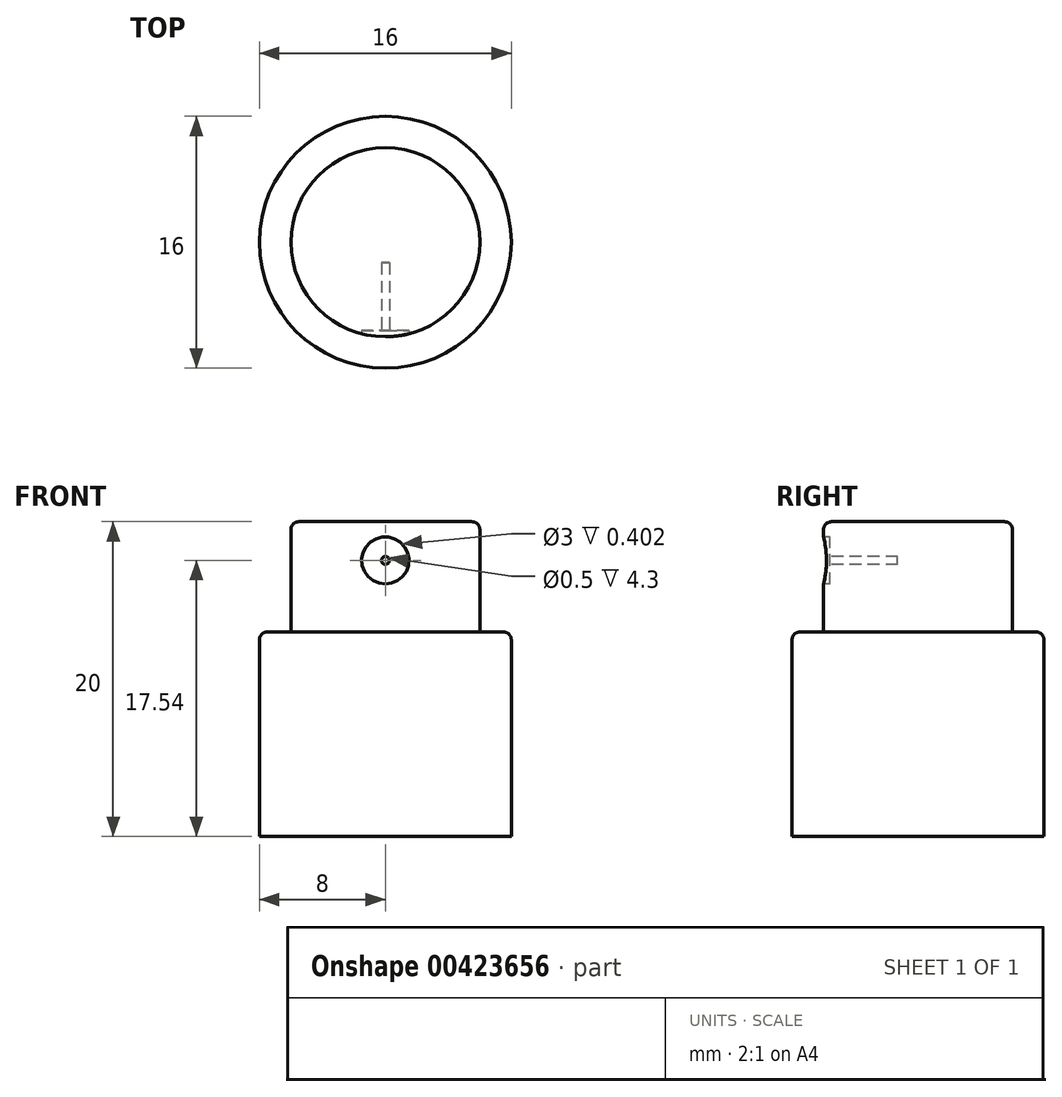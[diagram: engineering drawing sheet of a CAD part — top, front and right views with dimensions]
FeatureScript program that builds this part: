
annotation { "Feature Type Name" : "Feature", "Feature Type Description" : "" }
export const myFeature = defineFeature(function(context is Context, id is Id, definition is map)
    precondition{}
    {
        {
            var Q0;
            Q0=qCreatedBy(makeId("Top.planeOp"),FACE);
            var sketch = newSketch(context, id + "F0", { "sketchPlane" : qUnion([Q0])});
            skCircle(sketch, "E0", {"center": v(0, 0) * mm, "radius": 8 * mm});
            skCircle(sketch, "E1", {"center": v(0, 0) * mm, "radius": 6 * mm});
            skSolve(sketch);
        }
        {
            var Q0;
            Q0=makeQuery(id+"F0.imprint","IMPRINT",FACE,{"disambiguationData":[TD([[makeQuery(id+"F0.imprint","IMPRINT",EDGE,{"derivedFrom":sQuery(id+"F0.wireOp",EDGE,"E1")}),1.0]])]});
            extrude(context, id + "F1", {"entities" : qUnion([Q0]), "depth" : 20 * mm});
        }
        {
            var Q0;
            Q0=qSketchRegion(id+"F0",true);
            extrude(context, id + "F2", {"entities" : qUnion([Q0]), "operationType" : NewBodyOperationType.ADD, "depth" : 13 * mm});
        }
        {
            var Q0;
            Q0=qCreatedBy(makeId("Front.planeOp"),FACE);
            cPlane(context, id + "F3", {"entities" : qUnion([Q0]), "cplaneType" : CPlaneType.OFFSET, "offset" : 25 * mm, "width" : 150 * mm, "height" : 150 * mm});
        }
        {
            var Q0;
            Q0=qCreatedBy(id+"F3.planeOp",FACE);
            var sketch = newSketch(context, id + "F4", { "sketchPlane" : qUnion([Q0])});
            skCircle(sketch, "E2", {"center": v(0, 17.54) * mm, "radius": 1.5 * mm});
            skCircle(sketch, "E3", {"center": v(0, 17.54) * mm, "radius": 0.25 * mm});
            skSolve(sketch);
        }
        {
            var Q0;
            Q0=makeQuery(id+"F4.imprint","IMPRINT",FACE,{"disambiguationData":[TD([[makeQuery(id+"F4.imprint","IMPRINT",EDGE,{"derivedFrom":sQuery(id+"F4.wireOp",EDGE,"E3")}),1.0]])]});
            extrude(context, id + "F5", {"entities" : qUnion([Q0]), "operationType" : NewBodyOperationType.REMOVE, "oppositeDirection" : true, "depth" : 23.7 * mm});
        }
        {
            var Q0;
            Q0=qSketchRegion(id+"F4",true);
            extrude(context, id + "F6", {"entities" : qUnion([Q0]), "operationType" : NewBodyOperationType.REMOVE, "oppositeDirection" : true, "depth" : 19.4 * mm});
        }
        {
            var Q0;
            Q0=makeQuery(id+"F2.opExtrude","CAP_EDGE",EDGE,{"disambiguationData":[OSD([sQuery(id+"F0.wireOp",EDGE,"E0")])],"isStart":false});
            var Q1;
            Q1=makeQuery(id+"F1.opExtrude","CAP_EDGE",EDGE,{"disambiguationData":[OSD([sQuery(id+"F0.wireOp",EDGE,"E1")])],"isStart":false});
            fillet(context, id + "F7", {"entities" : qUnion([Q0, Q1]), "radius" : 0.5 * mm, "tangentPropagation" : true, "allowEdgeOverflow" : false});
        }
    });
